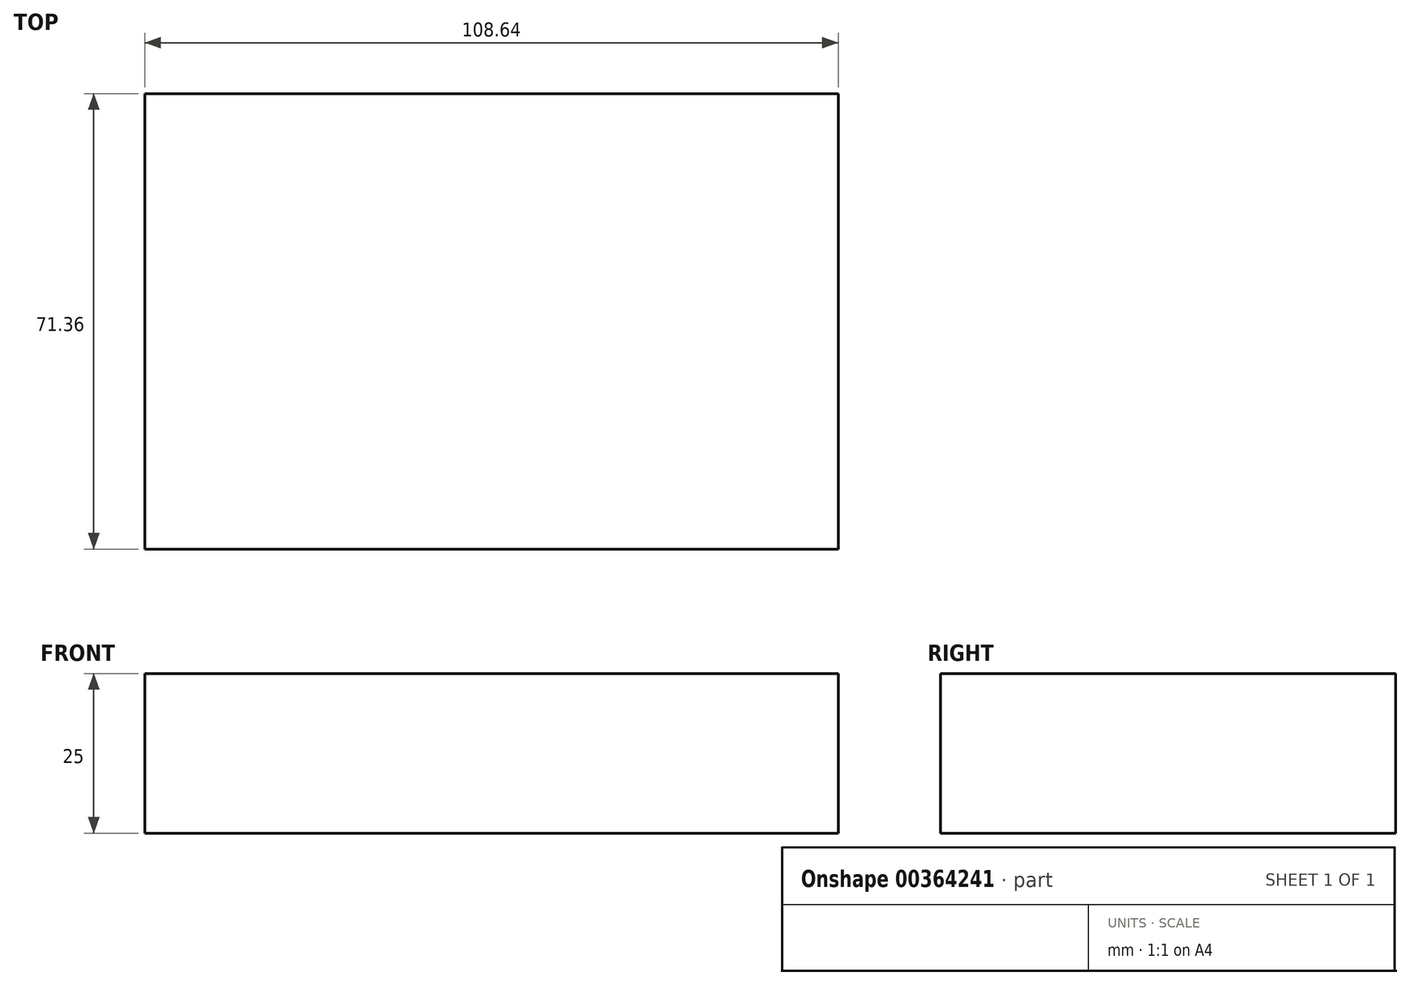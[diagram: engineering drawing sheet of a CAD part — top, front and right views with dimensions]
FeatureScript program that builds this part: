
annotation { "Feature Type Name" : "Feature", "Feature Type Description" : "" }
export const myFeature = defineFeature(function(context is Context, id is Id, definition is map)
    precondition{}
    {
        {
            var Q0;
            Q0=qCreatedBy(makeId("Top.planeOp"),FACE);
            var sketch = newSketch(context, id + "F0", { "sketchPlane" : qUnion([Q0])});
            skLineSegment(sketch, "E0.bottom", {"start": v(-54.32, 35.68) * mm, "end": v(54.32, 35.68) * mm});
            skLineSegment(sketch, "E0.top", {"start": v(-54.32, -35.68) * mm, "end": v(54.32, -35.68) * mm});
            skLineSegment(sketch, "E0.left", {"start": v(-54.32, 35.68) * mm, "end": v(-54.32, -35.68) * mm});
            skLineSegment(sketch, "E0.right", {"start": v(54.32, 35.68) * mm, "end": v(54.32, -35.68) * mm});
            skPoint(sketch, "E0.middle", {"position": v(0, 0) * mm});
            skSolve(sketch);
        }
        {
            var Q0;
            Q0 = qSketchRegion(id + "F0", true);
            extrude(context, id + "F1", {"entities" : qUnion([Q0]), "depth" : 25 * mm});
        }
    });
